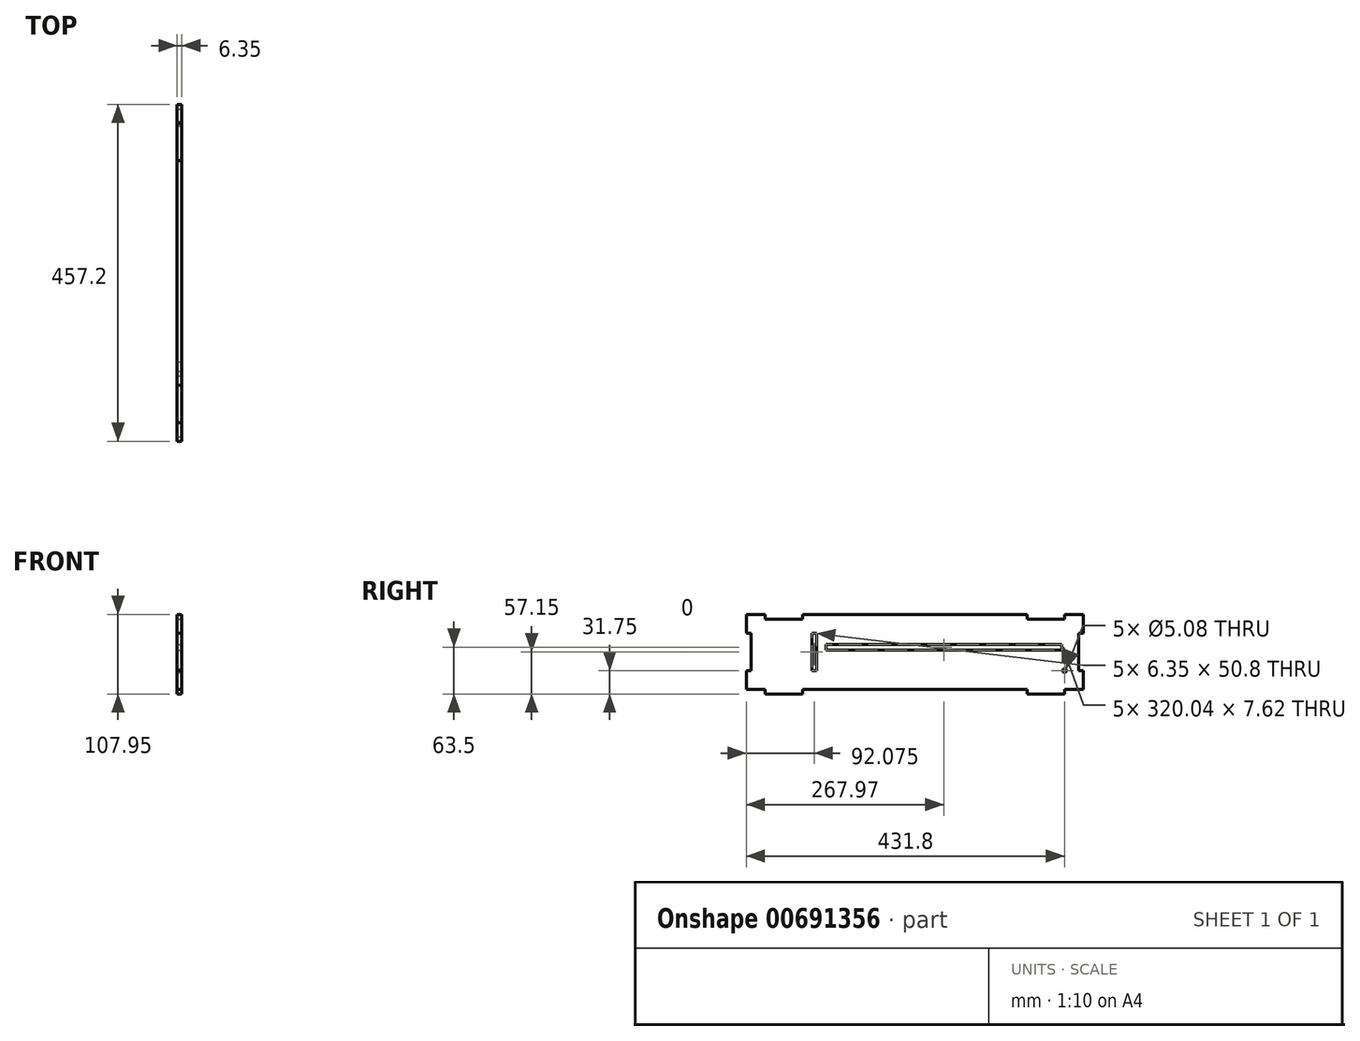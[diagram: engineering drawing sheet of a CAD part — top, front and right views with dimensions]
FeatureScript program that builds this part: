
annotation { "Feature Type Name" : "Feature", "Feature Type Description" : "" }
export const myFeature = defineFeature(function(context is Context, id is Id, definition is map)
    precondition{}
    {
        {
            var Q0;
            Q0=qCreatedBy(makeId("Right.planeOp"),FACE);
            var sketch = newSketch(context, id + "F0", { "sketchPlane" : qUnion([Q0])});
            skLineSegment(sketch, "E0.bottom", {"start": v(-228.6, 101.6) * mm, "end": v(228.6, 101.6) * mm});
            skLineSegment(sketch, "E0.top", {"start": v(-228.6, 0) * mm, "end": v(228.6, 0) * mm});
            skLineSegment(sketch, "E0.left", {"start": v(-228.6, 101.6) * mm, "end": v(-228.6, 0) * mm});
            skLineSegment(sketch, "E0.right", {"start": v(228.6, 101.6) * mm, "end": v(228.6, 0) * mm});
            skSolve(sketch);
        }
        {
            var Q0;
            Q0=qSketchRegion(id+"F0",true);
            extrude(context, id + "F1", {"entities" : qUnion([Q0]), "depth" : 6.35 * mm, "offsetDistance" : 25.4 * mm});
        }
        {
            var Q0;
            Q0=makeQuery(id+"F1.opExtrude","CAP_FACE",FACE,{"disambiguationData":[OSD([sQuery(id+"F0.wireOp",EDGE,"E0.bottom"),sQuery(id+"F0.wireOp",EDGE,"E0.top"),sQuery(id+"F0.wireOp",EDGE,"E0.left"),sQuery(id+"F0.wireOp",EDGE,"E0.right")])],"isStart":false});
            var sketch = newSketch(context, id + "F2", { "sketchPlane" : qUnion([Q0])});
            skLineSegment(sketch, "E1.bottom", {"start": v(203.2, 0) * mm, "end": v(152.4, 0) * mm});
            skLineSegment(sketch, "E1.top", {"start": v(203.2, -6.35) * mm, "end": v(152.4, -6.35) * mm});
            skLineSegment(sketch, "E1.left", {"start": v(203.2, 0) * mm, "end": v(203.2, -6.35) * mm});
            skLineSegment(sketch, "E1.right", {"start": v(152.4, 0) * mm, "end": v(152.4, -6.35) * mm});
            skLineSegment(sketch, "E2.MirrorCS", {"start": v(-152.4, 0) * mm, "end": v(-152.4, -6.35) * mm});
            skLineSegment(sketch, "E3.MirrorCS", {"start": v(-203.2, 0) * mm, "end": v(-203.2, -6.35) * mm});
            skLineSegment(sketch, "E4.MirrorCS", {"start": v(-203.2, 0) * mm, "end": v(-152.4, 0) * mm});
            skLineSegment(sketch, "E5.MirrorCS", {"start": v(-203.2, -6.35) * mm, "end": v(-152.4, -6.35) * mm});
            skSolve(sketch);
        }
        {
            var Q0;
            Q0=qSketchRegion(id+"F2",true);
            extrude(context, id + "F3", {"entities" : qUnion([Q0]), "oppositeDirection" : true, "depth" : 6.35 * mm, "offsetDistance" : 25.4 * mm});
        }
        {
            var Q0;
            Q0=makeQuery(id+"F1.opExtrude","CAP_FACE",FACE,{"disambiguationData":[OSD([sQuery(id+"F0.wireOp",EDGE,"E0.bottom"),sQuery(id+"F0.wireOp",EDGE,"E0.top"),sQuery(id+"F0.wireOp",EDGE,"E0.left"),sQuery(id+"F0.wireOp",EDGE,"E0.right")])],"isStart":false});
            var sketch = newSketch(context, id + "F4", { "sketchPlane" : qUnion([Q0])});
            skLineSegment(sketch, "E6", {"start": v(203.2, 0) * mm, "end": v(203.2, 25.4) * mm, "construction": true});
            skLineSegment(sketch, "E7", {"start": v(203.2, 25.4) * mm, "end": v(228.6, 25.4) * mm, "construction": true});
            skCircle(sketch, "E8", {"center": v(203.2, 25.4) * mm, "radius": 2.54 * mm});
            skLineSegment(sketch, "E9", {"start": v(-190.5, 0) * mm, "end": v(-190.5, 25.4) * mm, "construction": true});
            skLineSegment(sketch, "E10", {"start": v(-190.5, 25.4) * mm, "end": v(-228.6, 25.4) * mm, "construction": true});
            skCircle(sketch, "E11", {"center": v(-190.5, 25.4) * mm, "radius": 1.9 * mm, "construction": true});
            skSolve(sketch);
        }
        {
            var Q0;
            Q0=qSketchRegion(id+"F4",true);
            extrude(context, id + "F5", {"entities" : qUnion([Q0]), "operationType" : NewBodyOperationType.REMOVE, "endBound" : BoundingType.THROUGH_ALL, "oppositeDirection" : true, "depth" : 25.4 * mm, "offsetDistance" : 25.4 * mm});
        }
        {
            var Q0;
            Q0=makeQuery(id+"F1.opExtrude","CAP_FACE",FACE,{"disambiguationData":[OSD([sQuery(id+"F0.wireOp",EDGE,"E0.bottom"),sQuery(id+"F0.wireOp",EDGE,"E0.top"),sQuery(id+"F0.wireOp",EDGE,"E0.left"),sQuery(id+"F0.wireOp",EDGE,"E0.right")])],"isStart":false});
            var sketch = newSketch(context, id + "F6", { "sketchPlane" : qUnion([Q0])});
            skLineSegment(sketch, "E12.bottom", {"start": v(228.6, 76.2) * mm, "end": v(222.25, 76.2) * mm});
            skLineSegment(sketch, "E12.top", {"start": v(228.6, 25.4) * mm, "end": v(222.25, 25.4) * mm});
            skLineSegment(sketch, "E12.left", {"start": v(228.6, 76.2) * mm, "end": v(228.6, 25.4) * mm});
            skLineSegment(sketch, "E12.right", {"start": v(222.25, 76.2) * mm, "end": v(222.25, 25.4) * mm});
            skLineSegment(sketch, "E13.MirrorCS", {"start": v(-228.6, 76.2) * mm, "end": v(-222.25, 76.2) * mm});
            skLineSegment(sketch, "E14.MirrorCS", {"start": v(-228.6, 25.4) * mm, "end": v(-222.25, 25.4) * mm});
            skLineSegment(sketch, "E15.MirrorCS", {"start": v(-228.6, 76.2) * mm, "end": v(-228.6, 25.4) * mm});
            skLineSegment(sketch, "E16.MirrorCS", {"start": v(-222.25, 76.2) * mm, "end": v(-222.25, 25.4) * mm});
            skSolve(sketch);
        }
        {
            var Q0;
            Q0=qSketchRegion(id+"F6",true);
            extrude(context, id + "F7", {"entities" : qUnion([Q0]), "operationType" : NewBodyOperationType.REMOVE, "oppositeDirection" : true, "depth" : 25.4 * mm, "offsetDistance" : 25.4 * mm});
        }
        {
            var Q0;
            Q0=makeQuery(id+"F3.opExtrude","SWEPT_BODY",BODY,{"disambiguationData":[OSD([sQuery(id+"F2.wireOp",EDGE,"E2.MirrorCS"),sQuery(id+"F2.wireOp",EDGE,"E3.MirrorCS"),sQuery(id+"F2.wireOp",EDGE,"E4.MirrorCS"),sQuery(id+"F2.wireOp",EDGE,"E5.MirrorCS")])]});
            var Q1;
            Q1=makeQuery(id+"F1.opExtrude","SWEPT_BODY",BODY,{"disambiguationData":[OSD([sQuery(id+"F0.wireOp",EDGE,"E0.bottom"),sQuery(id+"F0.wireOp",EDGE,"E0.top"),sQuery(id+"F0.wireOp",EDGE,"E0.left"),sQuery(id+"F0.wireOp",EDGE,"E0.right")])]});
            var Q2;
            Q2=makeQuery(id+"F3.opExtrude","SWEPT_BODY",BODY,{"disambiguationData":[OSD([sQuery(id+"F2.wireOp",EDGE,"E1.bottom"),sQuery(id+"F2.wireOp",EDGE,"E1.top"),sQuery(id+"F2.wireOp",EDGE,"E1.left"),sQuery(id+"F2.wireOp",EDGE,"E1.right")])]});
            booleanBodies(context, id + "F8", {"operationType" : BooleanOperationType.UNION, "tools" : qUnion([Q0, Q1, Q2])});
        }
        {
            var Q0;
            Q0=makeQuery(id+"F8.opBoolean","MERGE",FACE,{"derivedFrom":[makeQuery(id+"F3.opExtrude","CAP_FACE",FACE,{"disambiguationData":[OSD([sQuery(id+"F2.wireOp",EDGE,"E1.bottom"),sQuery(id+"F2.wireOp",EDGE,"E1.top"),sQuery(id+"F2.wireOp",EDGE,"E1.left"),sQuery(id+"F2.wireOp",EDGE,"E1.right")])],"isStart":true}),makeQuery(id+"F3.opExtrude","CAP_FACE",FACE,{"disambiguationData":[OSD([sQuery(id+"F2.wireOp",EDGE,"E2.MirrorCS"),sQuery(id+"F2.wireOp",EDGE,"E3.MirrorCS"),sQuery(id+"F2.wireOp",EDGE,"E4.MirrorCS"),sQuery(id+"F2.wireOp",EDGE,"E5.MirrorCS")])],"isStart":true}),makeQuery(id+"F1.opExtrude","CAP_FACE",FACE,{"disambiguationData":[OSD([sQuery(id+"F0.wireOp",EDGE,"E0.bottom"),sQuery(id+"F0.wireOp",EDGE,"E0.top"),sQuery(id+"F0.wireOp",EDGE,"E0.left"),sQuery(id+"F0.wireOp",EDGE,"E0.right")])],"isStart":false})]});
            var sketch = newSketch(context, id + "F9", { "sketchPlane" : qUnion([Q0])});
            skLineSegment(sketch, "E17.bottom", {"start": v(-139.7, 76.2) * mm, "end": v(-133.35, 76.2) * mm});
            skLineSegment(sketch, "E17.top", {"start": v(-139.7, 25.4) * mm, "end": v(-133.35, 25.4) * mm});
            skLineSegment(sketch, "E17.left", {"start": v(-139.7, 76.2) * mm, "end": v(-139.7, 25.4) * mm});
            skLineSegment(sketch, "E17.right", {"start": v(-133.35, 76.2) * mm, "end": v(-133.35, 25.4) * mm});
            skSolve(sketch);
        }
        {
            var Q0;
            Q0=qSketchRegion(id+"F9",true);
            extrude(context, id + "F10", {"entities" : qUnion([Q0]), "operationType" : NewBodyOperationType.REMOVE, "oppositeDirection" : true, "depth" : 25.4 * mm, "offsetDistance" : 25.4 * mm});
        }
        {
            var Q0;
            Q0=makeQuery(id+"F8.opBoolean","MERGE",FACE,{"derivedFrom":[makeQuery(id+"F3.opExtrude","CAP_FACE",FACE,{"disambiguationData":[OSD([sQuery(id+"F2.wireOp",EDGE,"E1.bottom"),sQuery(id+"F2.wireOp",EDGE,"E1.top"),sQuery(id+"F2.wireOp",EDGE,"E1.left"),sQuery(id+"F2.wireOp",EDGE,"E1.right")])],"isStart":true}),makeQuery(id+"F3.opExtrude","CAP_FACE",FACE,{"disambiguationData":[OSD([sQuery(id+"F2.wireOp",EDGE,"E2.MirrorCS"),sQuery(id+"F2.wireOp",EDGE,"E3.MirrorCS"),sQuery(id+"F2.wireOp",EDGE,"E4.MirrorCS"),sQuery(id+"F2.wireOp",EDGE,"E5.MirrorCS")])],"isStart":true}),makeQuery(id+"F1.opExtrude","CAP_FACE",FACE,{"disambiguationData":[OSD([sQuery(id+"F0.wireOp",EDGE,"E0.bottom"),sQuery(id+"F0.wireOp",EDGE,"E0.top"),sQuery(id+"F0.wireOp",EDGE,"E0.left"),sQuery(id+"F0.wireOp",EDGE,"E0.right")])],"isStart":false})]});
            var sketch = newSketch(context, id + "F11", { "sketchPlane" : qUnion([Q0])});
            skLineSegment(sketch, "E18.bottom", {"start": v(-203.2, 101.6) * mm, "end": v(-152.4, 101.6) * mm});
            skLineSegment(sketch, "E18.top", {"start": v(-203.2, 95.25) * mm, "end": v(-152.4, 95.25) * mm});
            skLineSegment(sketch, "E18.left", {"start": v(-203.2, 101.6) * mm, "end": v(-203.2, 95.25) * mm});
            skLineSegment(sketch, "E18.right", {"start": v(-152.4, 101.6) * mm, "end": v(-152.4, 95.25) * mm});
            skLineSegment(sketch, "E19.MirrorCS", {"start": v(152.4, 101.6) * mm, "end": v(152.4, 95.25) * mm});
            skLineSegment(sketch, "E20.MirrorCS", {"start": v(203.2, 101.6) * mm, "end": v(203.2, 95.25) * mm});
            skLineSegment(sketch, "E21.MirrorCS", {"start": v(203.2, 95.25) * mm, "end": v(152.4, 95.25) * mm});
            skLineSegment(sketch, "E22.MirrorCS", {"start": v(203.2, 101.6) * mm, "end": v(152.4, 101.6) * mm});
            skSolve(sketch);
        }
        {
            var Q0;
            Q0=qSketchRegion(id+"F11",true);
            extrude(context, id + "F12", {"entities" : qUnion([Q0]), "operationType" : NewBodyOperationType.REMOVE, "oppositeDirection" : true, "depth" : 25.4 * mm, "offsetDistance" : 25.4 * mm});
        }
        {
            var Q0;
            Q0=makeQuery(id+"F8.opBoolean","MERGE",FACE,{"derivedFrom":[makeQuery(id+"F3.opExtrude","CAP_FACE",FACE,{"disambiguationData":[OSD([sQuery(id+"F2.wireOp",EDGE,"E1.bottom"),sQuery(id+"F2.wireOp",EDGE,"E1.top"),sQuery(id+"F2.wireOp",EDGE,"E1.left"),sQuery(id+"F2.wireOp",EDGE,"E1.right")])],"isStart":true}),makeQuery(id+"F3.opExtrude","CAP_FACE",FACE,{"disambiguationData":[OSD([sQuery(id+"F2.wireOp",EDGE,"E2.MirrorCS"),sQuery(id+"F2.wireOp",EDGE,"E3.MirrorCS"),sQuery(id+"F2.wireOp",EDGE,"E4.MirrorCS"),sQuery(id+"F2.wireOp",EDGE,"E5.MirrorCS")])],"isStart":true}),makeQuery(id+"F1.opExtrude","CAP_FACE",FACE,{"disambiguationData":[OSD([sQuery(id+"F0.wireOp",EDGE,"E0.bottom"),sQuery(id+"F0.wireOp",EDGE,"E0.top"),sQuery(id+"F0.wireOp",EDGE,"E0.left"),sQuery(id+"F0.wireOp",EDGE,"E0.right")])],"isStart":false})]});
            var sketch = newSketch(context, id + "F13", { "sketchPlane" : qUnion([Q0])});
            skLineSegment(sketch, "E23.bottom", {"start": v(-120.65, 60.96) * mm, "end": v(199.39, 60.96) * mm});
            skLineSegment(sketch, "E23.top", {"start": v(-120.65, 53.34) * mm, "end": v(199.39, 53.34) * mm});
            skLineSegment(sketch, "E23.left", {"start": v(-120.65, 60.96) * mm, "end": v(-120.65, 53.34) * mm});
            skLineSegment(sketch, "E23.right", {"start": v(199.39, 60.96) * mm, "end": v(199.39, 53.34) * mm});
            skSolve(sketch);
        }
        {
            var Q0;
            Q0=qSketchRegion(id+"F13",true);
            extrude(context, id + "F14", {"entities" : qUnion([Q0]), "operationType" : NewBodyOperationType.REMOVE, "oppositeDirection" : true, "depth" : 25.4 * mm, "offsetDistance" : 25.4 * mm});
        }
    });
